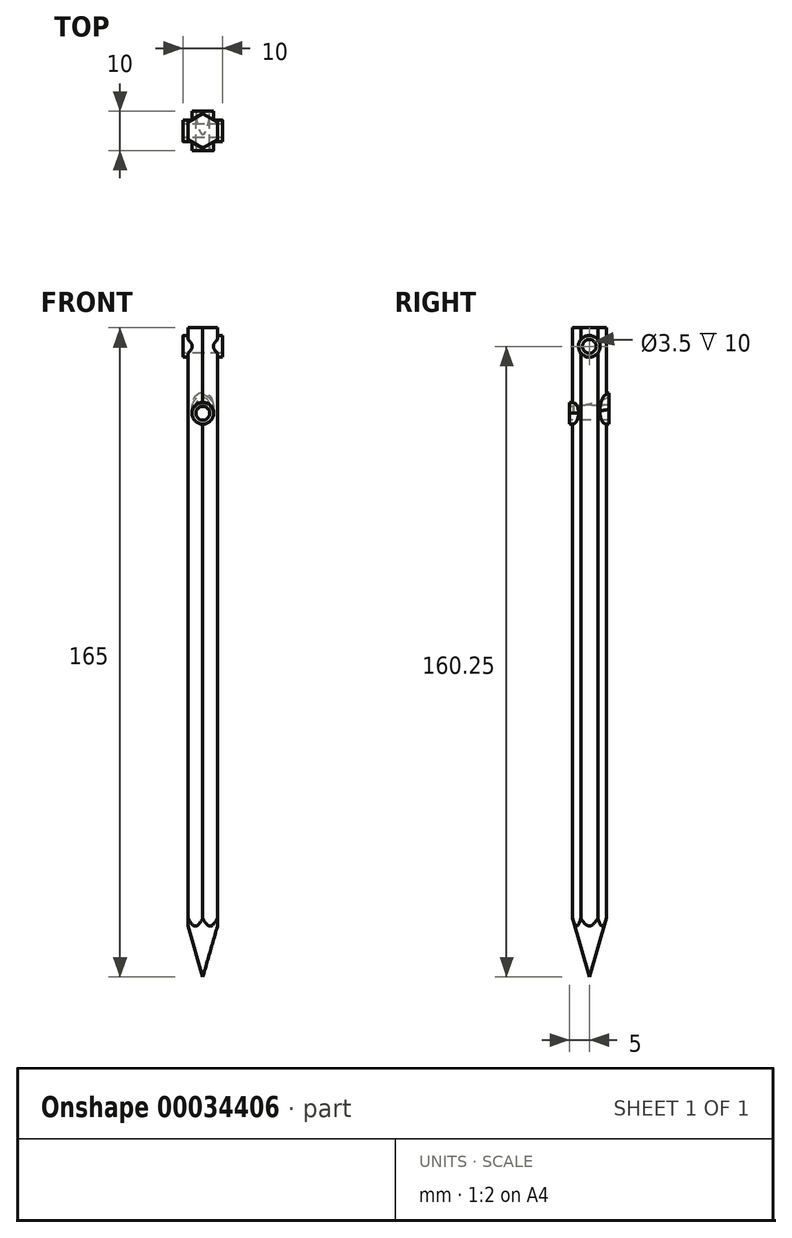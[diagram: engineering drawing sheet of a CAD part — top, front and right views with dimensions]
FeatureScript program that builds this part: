
annotation { "Feature Type Name" : "Feature", "Feature Type Description" : "" }
export const myFeature = defineFeature(function(context is Context, id is Id, definition is map)
    precondition{}
    {
        {
            var Q0;
            Q0=qCreatedBy(makeId("Top.planeOp"),FACE);
            var sketch = newSketch(context, id + "F0", { "sketchPlane" : qUnion([Q0])});
            skCircle(sketch, "E0.cCircle", {"center": v(0, 0) * mm, "radius": 3.75 * mm, "construction": true});
            skLineSegment(sketch, "E0.0", {"start": v(3.75, -2.17) * mm, "end": v(0, -4.33) * mm});
            skLineSegment(sketch, "E0.1", {"start": v(0, -4.33) * mm, "end": v(-3.75, -2.17) * mm});
            skLineSegment(sketch, "E0.2", {"start": v(-3.75, -2.17) * mm, "end": v(-3.75, 2.17) * mm});
            skLineSegment(sketch, "E0.3", {"start": v(-3.75, 2.17) * mm, "end": v(0, 4.33) * mm});
            skLineSegment(sketch, "E0.4", {"start": v(0, 4.33) * mm, "end": v(3.75, 2.17) * mm});
            skLineSegment(sketch, "E0.5", {"start": v(3.75, 2.17) * mm, "end": v(3.75, -2.17) * mm});
            skSolve(sketch);
        }
        {
            var Q0;
            Q0 = qSketchRegion(id + "F0", true);
            extrude(context, id + "F1", {"entities" : qUnion([Q0]), "depth" : 150 * mm});
        }
        {
            var Q0;
            Q0=qCreatedBy(makeId("Right.planeOp"),FACE);
            var sketch = newSketch(context, id + "F2", { "sketchPlane" : qUnion([Q0])});
            skLineSegment(sketch, "E1", {"start": v(0, 0) * mm, "end": v(4.33, 0) * mm});
            skLineSegment(sketch, "E2", {"start": v(4.33, 0) * mm, "end": v(0, -15) * mm});
            skLineSegment(sketch, "E3", {"start": v(0, -15) * mm, "end": v(0, 0) * mm});
            skSolve(sketch);
        }
        {
            var Q0;
            Q0 = qSketchRegion(id + "F2", true);
            var Q1;
            Q1=sQuery(id+"F2.wireOp",EDGE,"E3");
            revolve(context, id + "F3", {"operationType" : NewBodyOperationType.ADD, "entities" : qUnion([Q0]), "axis" : qUnion([Q1]), "revolveType" : RevolveType.FULL});
        }
        {
            var Q0;
            Q0=makeQuery(id+"F1.opExtrude","CAP_FACE",FACE,{"disambiguationData":[OSD([sQuery(id+"F0.wireOp",EDGE,"E0.0"),sQuery(id+"F0.wireOp",EDGE,"E0.1"),sQuery(id+"F0.wireOp",EDGE,"E0.2"),sQuery(id+"F0.wireOp",EDGE,"E0.3"),sQuery(id+"F0.wireOp",EDGE,"E0.4"),sQuery(id+"F0.wireOp",EDGE,"E0.5")])],"isStart":false});
            var sketch = newSketch(context, id + "F4", { "sketchPlane" : qUnion([Q0])});
            skCircle(sketch, "E4", {"center": v(0, 0) * mm, "radius": 9.63 * mm});
            skCircle(sketch, "E5.cCircle", {"center": v(0, 0) * mm, "radius": 3.75 * mm, "construction": true});
            skLineSegment(sketch, "E5.0", {"start": v(3.75, -2.17) * mm, "end": v(0, -4.33) * mm});
            skLineSegment(sketch, "E5.1", {"start": v(0, -4.33) * mm, "end": v(-3.75, -2.17) * mm});
            skLineSegment(sketch, "E5.2", {"start": v(-3.75, -2.17) * mm, "end": v(-3.75, 2.17) * mm});
            skLineSegment(sketch, "E5.3", {"start": v(-3.75, 2.17) * mm, "end": v(0, 4.33) * mm});
            skLineSegment(sketch, "E5.4", {"start": v(0, 4.33) * mm, "end": v(3.75, 2.17) * mm});
            skLineSegment(sketch, "E5.5", {"start": v(3.75, 2.17) * mm, "end": v(3.75, -2.17) * mm});
            skPoint(sketch, "E5.0.midPoint", {"position": v(1.88, -3.25) * mm});
            skSolve(sketch);
        }
        {
            var Q0;
            Q0 = qSketchRegion(id + "F4", true);
            extrude(context, id + "F5", {"entities" : qUnion([Q0]), "operationType" : NewBodyOperationType.REMOVE, "endBound" : BoundingType.THROUGH_ALL, "oppositeDirection" : true, "depth" : 25 * mm});
        }
        {
            var Q0;
            Q0=makeQuery(id+"F5.boolean.opBoolean","MERGE",FACE,{"derivedFrom":[makeQuery(id+"F1.opExtrude","SWEPT_FACE",FACE,{"disambiguationData":[OSD([sQuery(id+"F0.wireOp",EDGE,"E0.2")])]}),makeQuery(id+"F5.opExtrude","SWEPT_FACE",FACE,{"disambiguationData":[OSD([sQuery(id+"F4.wireOp",EDGE,"E5.2")])]})]});
            var sketch = newSketch(context, id + "F6", { "sketchPlane" : qUnion([Q0])});
            skCircle(sketch, "E6", {"center": v(0, 145.25) * mm, "radius": 1.75 * mm});
            skSolve(sketch);
        }
        {
            var Q0;
            Q0 = qSketchRegion(id + "F6", true);
            extrude(context, id + "F7", {"entities" : qUnion([Q0]), "operationType" : NewBodyOperationType.REMOVE, "endBound" : BoundingType.THROUGH_ALL, "oppositeDirection" : true, "depth" : 25 * mm});
        }
        {
            var Q0;
            Q0=qCreatedBy(makeId("Front.planeOp"),FACE);
            var sketch = newSketch(context, id + "F8", { "sketchPlane" : qUnion([Q0])});
            skCircle(sketch, "E7", {"center": v(0, 128.25) * mm, "radius": 1.75 * mm});
            skSolve(sketch);
        }
        {
            var Q0;
            Q0 = qSketchRegion(id + "F8", true);
            extrude(context, id + "F9", {"entities" : qUnion([Q0]), "operationType" : NewBodyOperationType.REMOVE, "endBound" : BoundingType.SYMMETRIC, "oppositeDirection" : true, "depth" : 25 * mm});
        }
        {
            var Q0;
            Q0=qCreatedBy(makeId("Front.planeOp"),FACE);
            var sketch = newSketch(context, id + "F10", { "sketchPlane" : qUnion([Q0])});
            skCircle(sketch, "E8", {"center": v(0, 128.25) * mm, "radius": 1.75 * mm});
            skCircle(sketch, "E9", {"center": v(0, 128.25) * mm, "radius": 2.75 * mm});
            skSolve(sketch);
        }
        {
            var Q0;
            Q0 = qSketchRegion(id + "F10", true);
            extrude(context, id + "F11", {"entities" : qUnion([Q0]), "operationType" : NewBodyOperationType.ADD, "endBound" : BoundingType.SYMMETRIC, "depth" : 10 * mm});
        }
        {
            var Q0;
            Q0=qCreatedBy(makeId("Right.planeOp"),FACE);
            var sketch = newSketch(context, id + "F12", { "sketchPlane" : qUnion([Q0])});
            skCircle(sketch, "E10", {"center": v(0, 145.25) * mm, "radius": 2.75 * mm});
            skCircle(sketch, "E11", {"center": v(0, 145.25) * mm, "radius": 1.75 * mm});
            skSolve(sketch);
        }
        {
            var Q0;
            Q0 = qSketchRegion(id + "F12", true);
            extrude(context, id + "F13", {"entities" : qUnion([Q0]), "operationType" : NewBodyOperationType.ADD, "endBound" : BoundingType.SYMMETRIC, "depth" : 10 * mm});
        }
        {
            var Q0;
            Q0=makeQuery(id+"F11.opExtrude","CAP_FACE",FACE,{"disambiguationData":[OSD([sQuery(id+"F10.wireOp",EDGE,"E8"),sQuery(id+"F10.wireOp",EDGE,"E9")])],"isStart":false});
            var sketch = newSketch(context, id + "F14", { "sketchPlane" : qUnion([Q0])});
            skCircle(sketch, "E12", {"center": v(0, 128.25) * mm, "radius": 1.75 * mm});
            skSolve(sketch);
        }
        {
            var Q0;
            Q0=qCreatedBy(makeId("Right.planeOp"),FACE);
            cPlane(context, id + "F15", {"entities" : qUnion([Q0]), "cplaneType" : CPlaneType.OFFSET, "offset" : 3.5 * mm, "oppositeDirection" : true, "width" : 150 * mm, "height" : 150 * mm});
        }
        {
            var Q0;
            Q0=qCreatedBy(id+"F15.planeOp",FACE);
            var sketch = newSketch(context, id + "F16", { "sketchPlane" : qUnion([Q0])});
            skArc(sketch, "E13", {"start": v(-5, 128.25) * mm, "mid": v(12.66, 135.6) * mm, "end": v(20, 153.25) * mm});
            skSolve(sketch);
        }
        {
            var Q0;
            Q0=makeQuery(id+"F11.opExtrude","CAP_FACE",FACE,{"disambiguationData":[OSD([sQuery(id+"F10.wireOp",EDGE,"E8"),sQuery(id+"F10.wireOp",EDGE,"E9")])],"isStart":false});
            var sketch = newSketch(context, id + "F17", { "sketchPlane" : qUnion([Q0])});
            skCircle(sketch, "E14", {"center": v(0, 128.25) * mm, "radius": 2.75 * mm});
            skSolve(sketch);
        }
        {
            var Q0;
            Q0 = qSketchRegion(id + "F17", true);
            var Q1;
            Q1 = qConstructionFilter(qBodyType(qCreatedBy(id + "F16" ,EDGE), BodyType.WIRE), ConstructionObject.NO);
            sweep(context, id + "F18", {"operationType" : NewBodyOperationType.ADD, "profiles" : qUnion([Q0]), "path" : qUnion([Q1])});
        }
        {
            var Q0;
            Q0=qCreatedBy(makeId("Right.planeOp"),FACE);
            var sketch = newSketch(context, id + "F19", { "sketchPlane" : qUnion([Q0])});
            skLineSegment(sketch, "E15.bottom", {"start": v(5, 153.33) * mm, "end": v(35.1, 153.17) * mm});
            skLineSegment(sketch, "E15.top", {"start": v(5, 105.73) * mm, "end": v(35.1, 105.73) * mm});
            skLineSegment(sketch, "E15.left", {"start": v(5, 153.33) * mm, "end": v(5, 105.73) * mm});
            skLineSegment(sketch, "E15.right", {"start": v(35.1, 153.17) * mm, "end": v(35.1, 105.73) * mm});
            skSolve(sketch);
        }
        {
            var Q0;
            Q0 = qSketchRegion(id + "F19", true);
            extrude(context, id + "F20", {"entities" : qUnion([Q0]), "operationType" : NewBodyOperationType.REMOVE, "endBound" : BoundingType.SYMMETRIC, "oppositeDirection" : true, "depth" : 25 * mm});
        }
        {
            var Q0;
            Q0 = qSketchRegion(id + "F14", true);
            var Q1;
            Q1 = qConstructionFilter(qBodyType(qCreatedBy(id + "F16" ,EDGE), BodyType.WIRE), ConstructionObject.NO);
            sweep(context, id + "F21", {"operationType" : NewBodyOperationType.REMOVE, "profiles" : qUnion([Q0]), "path" : qUnion([Q1])});
        }
        {
            var Q0;
            Q0 = qSketchRegion(id + "F14", true);
            extrude(context, id + "F22", {"entities" : qUnion([Q0]), "operationType" : NewBodyOperationType.REMOVE, "endBound" : BoundingType.SYMMETRIC, "oppositeDirection" : true, "depth" : 25 * mm});
        }
        {
            var Q0;
            Q0=makeQuery(id+"F20.boolean.opBoolean","MERGE",FACE,{"derivedFrom":[makeQuery(id+"F11.opExtrude","CAP_FACE",FACE,{"disambiguationData":[OSD([sQuery(id+"F10.wireOp",EDGE,"E8"),sQuery(id+"F10.wireOp",EDGE,"E9")])],"isStart":true}),makeQuery(id+"F20.opExtrude","SWEPT_FACE",FACE,{"disambiguationData":[OSD([sQuery(id+"F19.wireOp",EDGE,"E15.left")])]})]});
            var sketch = newSketch(context, id + "F23", { "sketchPlane" : qUnion([Q0])});
            skLineSegment(sketch, "E16", {"start": v(-1.75, 130.35) * mm, "end": v(-1.75, 128.25) * mm});
            skLineSegment(sketch, "E17", {"start": v(-1.75, 130.35) * mm, "end": v(1.75, 130.35) * mm});
            skLineSegment(sketch, "E18", {"start": v(1.75, 130.35) * mm, "end": v(1.75, 128.25) * mm});
            skLineSegment(sketch, "E19", {"start": v(-1.75, 128.25) * mm, "end": v(1.75, 128.25) * mm});
            skSolve(sketch);
        }
        {
            var Q0;
            Q0 = qSketchRegion(id + "F23", true);
            extrude(context, id + "F24", {"entities" : qUnion([Q0]), "operationType" : NewBodyOperationType.REMOVE, "oppositeDirection" : true, "depth" : 9 * mm});
        }
    });
